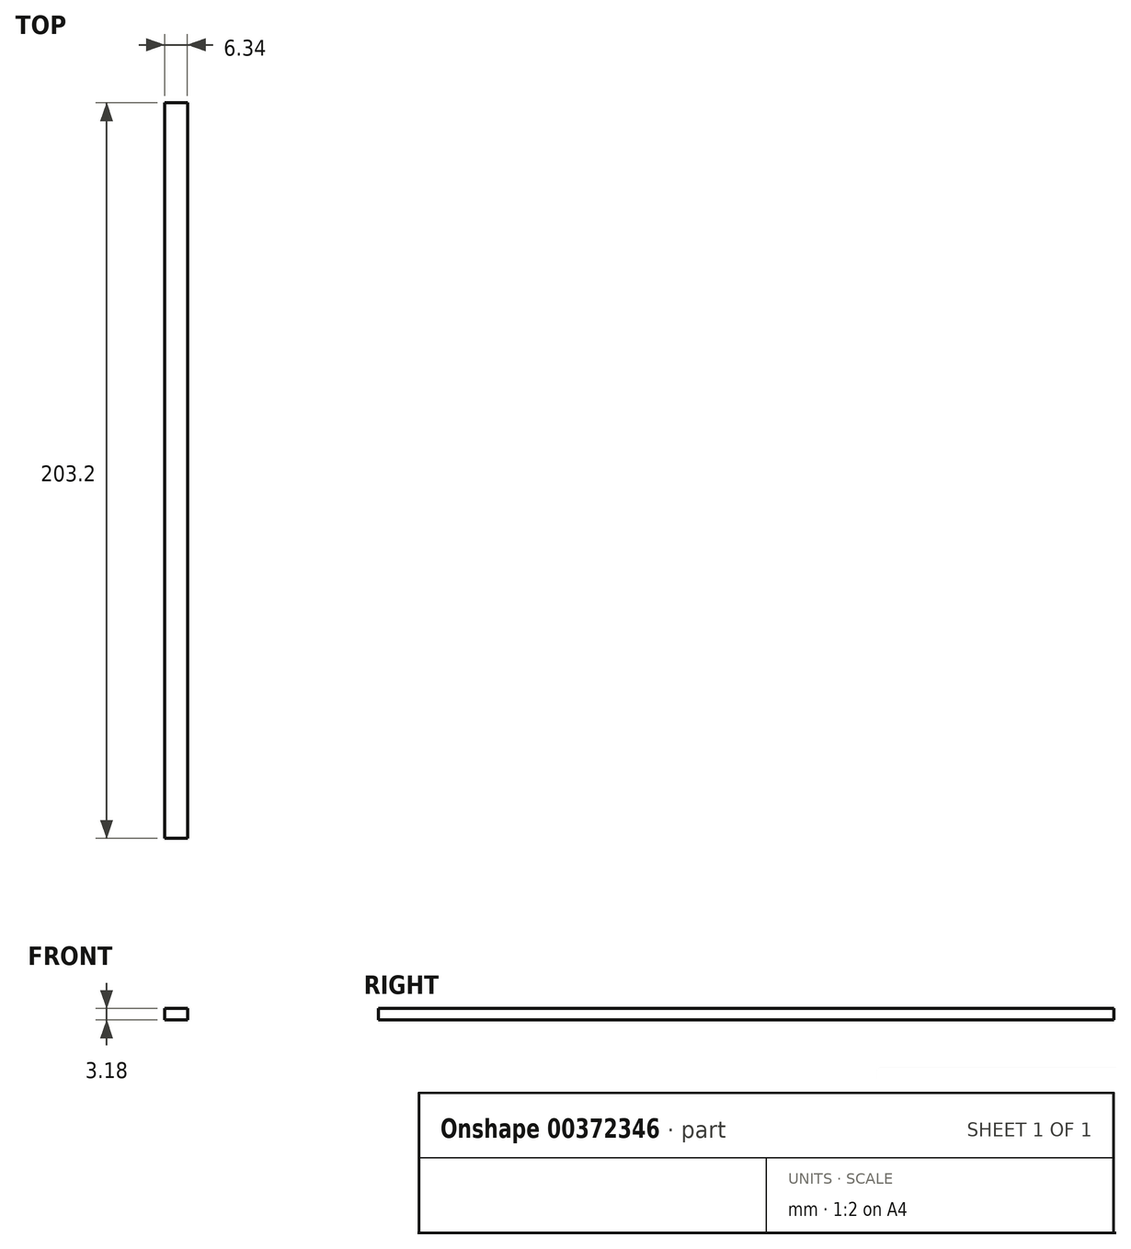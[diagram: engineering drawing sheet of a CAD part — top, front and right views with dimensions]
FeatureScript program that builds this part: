
annotation { "Feature Type Name" : "Feature", "Feature Type Description" : "" }
export const myFeature = defineFeature(function(context is Context, id is Id, definition is map)
    precondition{}
    {
        {
            var Q0;
            Q0=qCreatedBy(makeId("Front.planeOp"),FACE);
            var sketch = newSketch(context, id + "F0", { "sketchPlane" : qUnion([Q0])});
            skLineSegment(sketch, "E0.bottom", {"start": v(-3.18, -1.59) * mm, "end": v(3.18, -1.59) * mm});
            skLineSegment(sketch, "E0.top", {"start": v(-3.18, 1.59) * mm, "end": v(3.17, 1.59) * mm});
            skLineSegment(sketch, "E0.left", {"start": v(-3.18, -1.59) * mm, "end": v(-3.18, 1.59) * mm});
            skLineSegment(sketch, "E0.right", {"start": v(3.18, -1.59) * mm, "end": v(3.17, 1.59) * mm});
            skSolve(sketch);
        }
        {
            var Q0;
            Q0 = qSketchRegion(id + "F0", true);
            extrude(context, id + "F1", {"entities" : qUnion([Q0]), "endBound" : BoundingType.SYMMETRIC, "depth" : 203.2 * mm});
        }
    });
